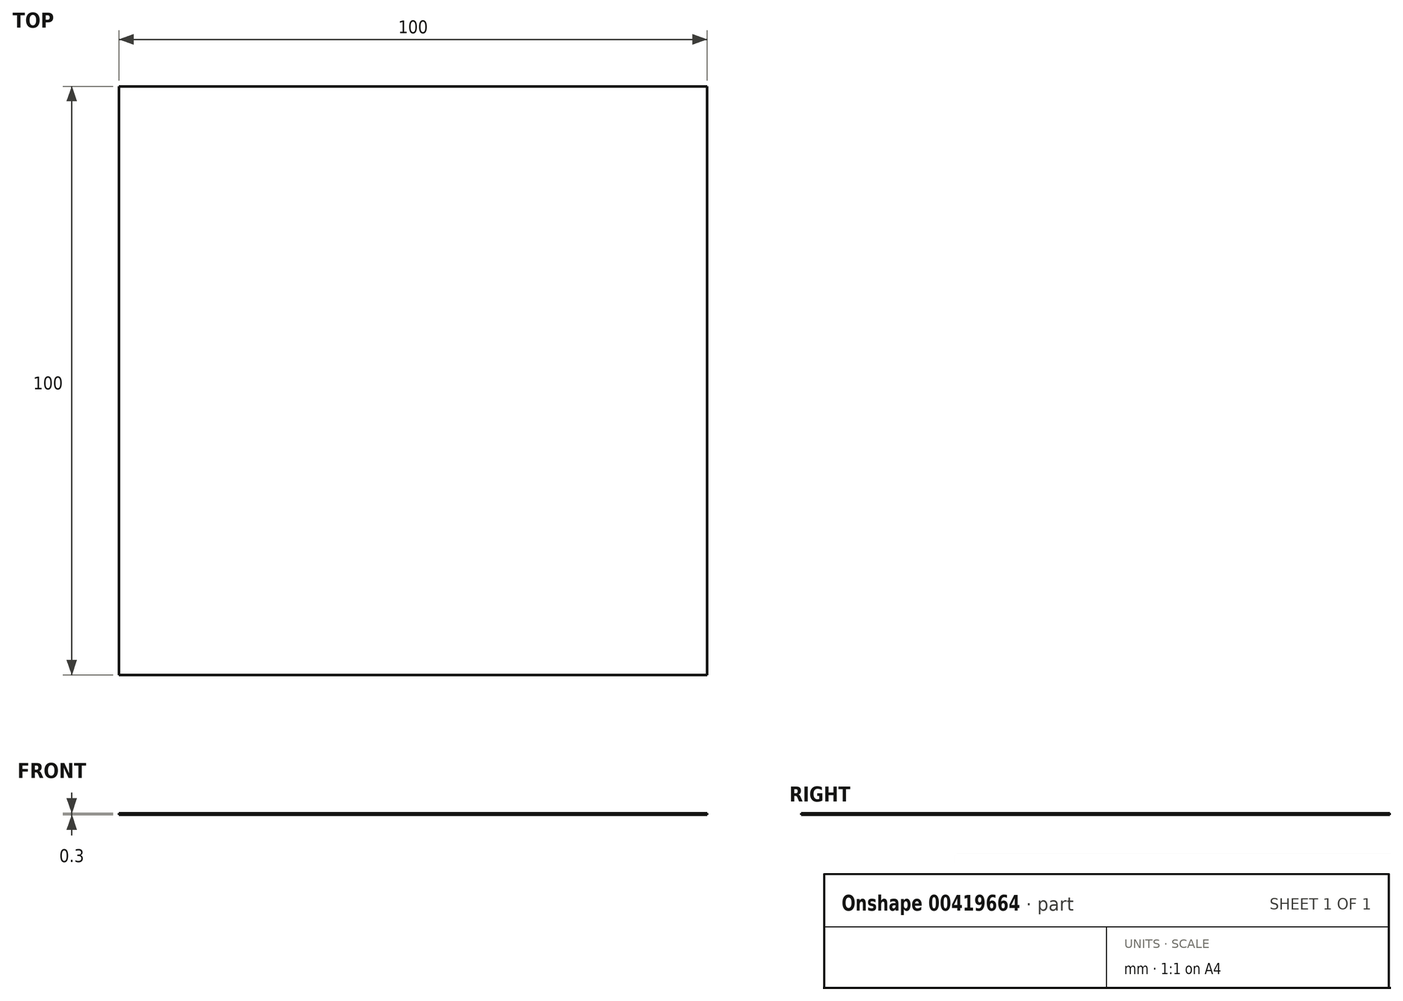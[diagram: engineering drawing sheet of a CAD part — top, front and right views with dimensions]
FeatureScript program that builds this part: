
annotation { "Feature Type Name" : "Feature", "Feature Type Description" : "" }
export const myFeature = defineFeature(function(context is Context, id is Id, definition is map)
    precondition{}
    {
        {
            var Q0;
            Q0=qCreatedBy(makeId("Top.planeOp"),FACE);
            var sketch = newSketch(context, id + "F0", { "sketchPlane" : qUnion([Q0])});
            skLineSegment(sketch, "E0.bottom", {"start": v(50, 50) * mm, "end": v(-50, 50) * mm});
            skLineSegment(sketch, "E0.top", {"start": v(50, -50) * mm, "end": v(-50, -50) * mm});
            skLineSegment(sketch, "E0.left", {"start": v(50, 50) * mm, "end": v(50, -50) * mm});
            skLineSegment(sketch, "E0.right", {"start": v(-50, 50) * mm, "end": v(-50, -50) * mm});
            skPoint(sketch, "E0.middle", {"position": v(0, 0) * mm});
            skSolve(sketch);
        }
        {
            var Q0;
            Q0=makeQuery(id+"F0.imprint","IMPRINT",FACE,{"disambiguationData":[TD([[makeQuery(id+"F0.imprint","IMPRINT",EDGE,{"derivedFrom":sQuery(id+"F0.wireOp",EDGE,"E0.bottom")}),1.0]])]});
            extrude(context, id + "F1", {"entities" : qUnion([Q0]), "depth" : .3 * mm});
        }
    });
